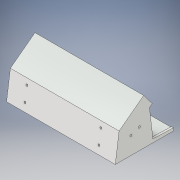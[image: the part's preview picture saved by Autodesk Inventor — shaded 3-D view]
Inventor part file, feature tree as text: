
AUTODESK INVENTOR PART (.ipt)
format: ipt  version: 2019 (Build 230136000, 136)  size: 218,112 bytes
history: native  units: in
note: dims shown in document units (in); Inventor stores cm internally (conversion verified against a paired STEP export)
features: extrude x4, sketch x4, plane x1, mirror x1, projected_geometry x1
ambient origin geometry x8: Origin, YZ Plane, XZ Plane, XY Plane, X Axis, Y Axis, Z Axis, Center Point
bodies: Solid1 (feature_tree)
feature tree (11):
  extrude  "Extrusion1"  Depth=1.5748in
  extrude  "Extrusion2"  Depth=1.7717in
  plane  "Work Plane1"
  mirror  "Mirror1"
  extrude  "Extrusion3"  Depth=0.8268in
  extrude  "Extrusion4"  Depth=0.3937in
  sketch  "Sketch1"  dims[d0=3.3465in d1=1.5748in]
  sketch  "Sketch2"  dims[d2=0.055in d3=1.7717in]
  projected_geometry  "Projected Loop1"
  sketch  "Sketch3"  dims[d4=135.0deg d5=0.8268in]
  sketch  "Sketch4"  dims[d6=0.1969in d7=0.5841in d10=0.1181in d11=0.0in d12=0.1575in d13=0.1969in d14=0.1181in d15=0.1181in d16=0.1181in d17=0.1181in d18=0.1181in d21=0.1181in d22=0.1181in d23=0.1181in d24=6.0236in d25=0.0in d28=1.0in d29=1.1811in d31=0.75in d32=1.2008in d33=0.1181in d34=0.1181in d35=7.874in d36=0.0in d37=0.4375in d38=1.25in d39=1.0in d40=1.25in d41=0.4375in d42=1.0in d43=0.1181in d44=0.1181in d45=0.1181in d46=0.1181in d47=0.3937in d48=0.0in d50=1.1811in]
